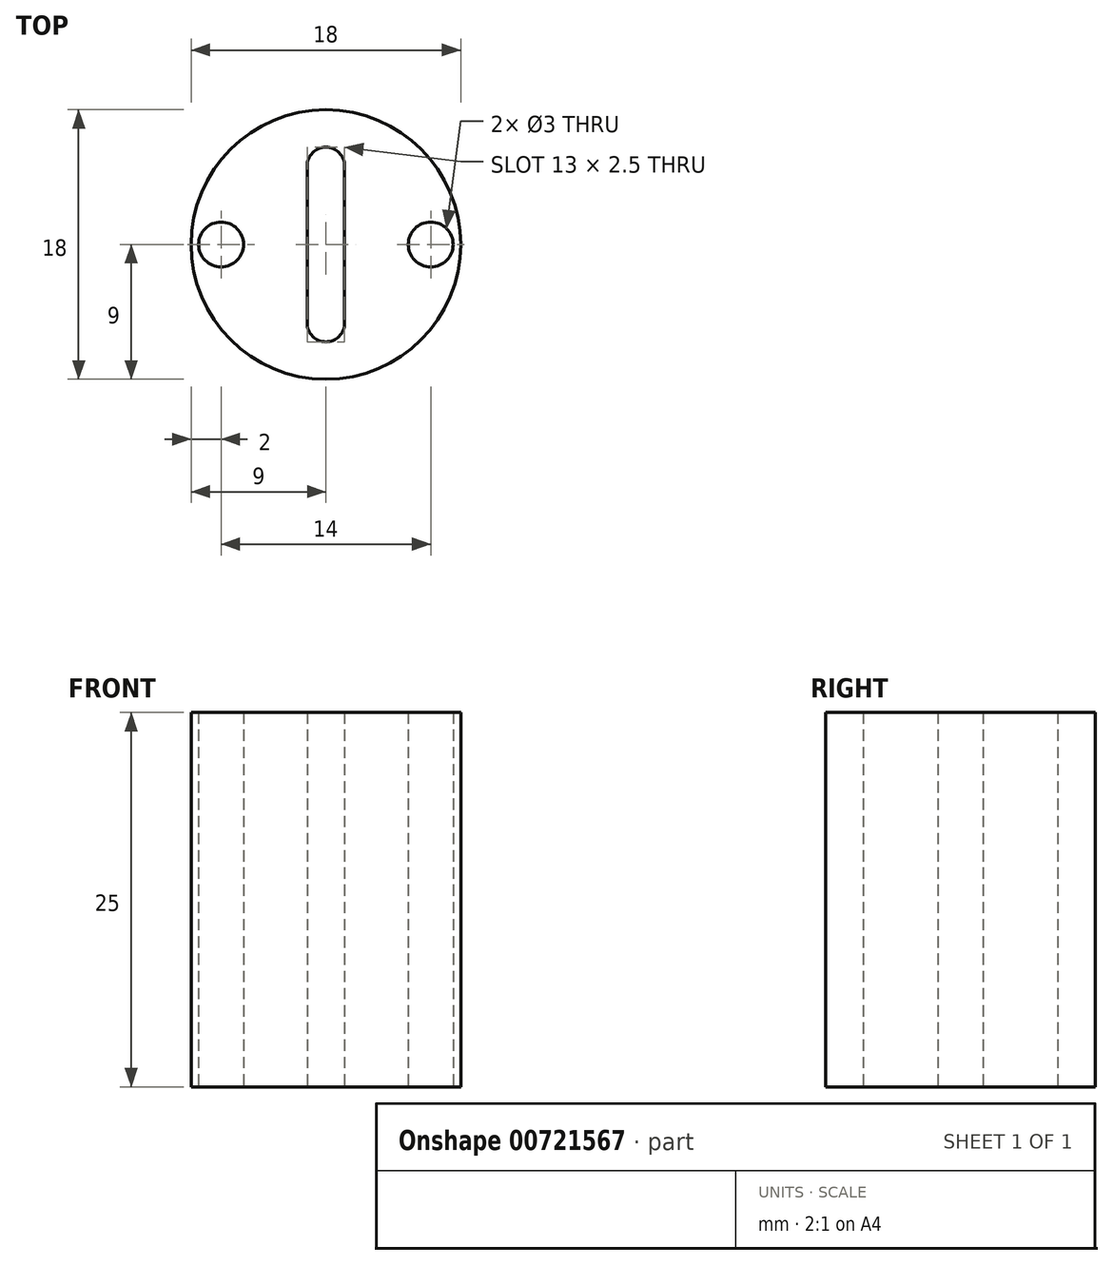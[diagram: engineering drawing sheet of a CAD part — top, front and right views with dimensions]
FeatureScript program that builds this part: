
annotation { "Feature Type Name" : "Feature", "Feature Type Description" : "" }
export const myFeature = defineFeature(function(context is Context, id is Id, definition is map)
    precondition{}
    {
        {
            var Q0;
            Q0=qCreatedBy(makeId("Top.planeOp"),FACE);
            var sketch = newSketch(context, id + "F0", { "sketchPlane" : qUnion([Q0])});
            skCircle(sketch, "E0", {"center": v(0, 0) * mm, "radius": 9 * mm});
            skLineSegment(sketch, "E1", {"start": v(0, 13.8) * mm, "end": v(0, 6.5) * mm, "construction": true});
            skLineSegment(sketch, "E2", {"start": v(-18.47, 0) * mm, "end": v(23.83, 0) * mm, "construction": true});
            skLineSegment(sketch, "E3", {"start": v(0, 9) * mm, "end": v(0, 6.5) * mm, "construction": true});
            skLineSegment(sketch, "E4", {"start": v(0, -9) * mm, "end": v(0, -6.5) * mm, "construction": true});
            skArc(sketch, "E5", {"start": v(1.25, 5.25) * mm, "mid": v(0, 6.5) * mm, "end": v(-1.25, 5.25) * mm});
            skArc(sketch, "E6", {"start": v(-1.25, -5.25) * mm, "mid": v(0, -6.5) * mm, "end": v(1.25, -5.25) * mm});
            skLineSegment(sketch, "E7", {"start": v(-1.25, -5.25) * mm, "end": v(-1.25, 5.25) * mm});
            skLineSegment(sketch, "E8", {"start": v(1.25, 5.25) * mm, "end": v(1.25, -5.25) * mm});
            skLineSegment(sketch, "E9.trimOffspring", {"start": v(0, -6.5) * mm, "end": v(0, -24.3) * mm, "construction": true});
            skLineSegment(sketch, "E10", {"start": v(-9, 0) * mm, "end": v(-8.5, 0) * mm, "construction": true});
            skLineSegment(sketch, "E11.MirrorCS", {"start": v(9, 0) * mm, "end": v(8.5, 0) * mm, "construction": true});
            skLineSegment(sketch, "E12", {"start": v(-8.5, 0) * mm, "end": v(-7, 0) * mm, "construction": true});
            skLineSegment(sketch, "E13.MirrorCS", {"start": v(8.5, 0) * mm, "end": v(7, 0) * mm, "construction": true});
            skCircle(sketch, "E14", {"center": v(-7, 0) * mm, "radius": 1.5 * mm});
            skCircle(sketch, "E15", {"center": v(7, 0) * mm, "radius": 1.5 * mm});
            skSolve(sketch);
        }
        {
            var Q0;
            Q0 = qSketchRegion(id + "F0", true);
            extrude(context, id + "F1", {"entities" : qUnion([Q0]), "depth" : 25 * mm, "offsetDistance" : 25 * mm});
        }
    });
